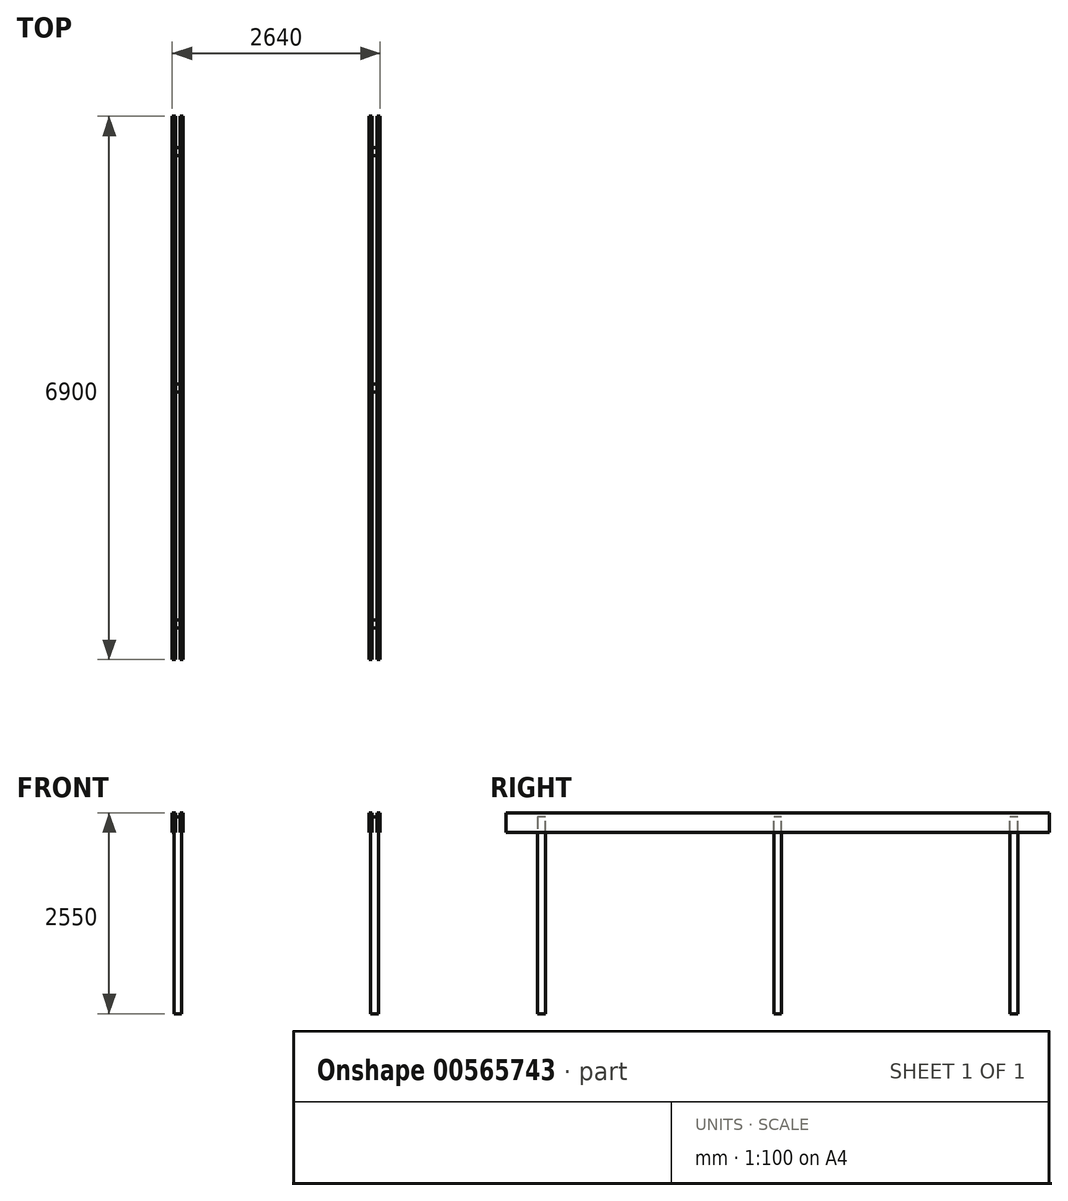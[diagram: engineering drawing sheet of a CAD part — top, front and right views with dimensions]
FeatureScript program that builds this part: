
annotation { "Feature Type Name" : "Feature", "Feature Type Description" : "" }
export const myFeature = defineFeature(function(context is Context, id is Id, definition is map)
    precondition{}
    {
        {
            assignVariable(context, id + "F0", {"name" : "Laenge", "anyValue" : 6000 * mm});
        }
        {
            assignVariable(context, id + "F1", {"name" : "Hoehe", "anyValue" : 2500});
        }
        {
            var Q0;
            Q0=qCreatedBy(makeId("Top.planeOp"),FACE);
            var sketch = newSketch(context, id + "F2", { "sketchPlane" : qUnion([Q0])});
            skLineSegment(sketch, "E0.bottom", {"start": v(-68.16, -102.24) * mm, "end": v(31.84, -102.24) * mm});
            skLineSegment(sketch, "E0.top", {"start": v(-68.16, -2.24) * mm, "end": v(31.84, -2.24) * mm});
            skLineSegment(sketch, "E0.left", {"start": v(-68.16, -102.24) * mm, "end": v(-68.16, -2.24) * mm});
            skLineSegment(sketch, "E0.right", {"start": v(31.84, -102.24) * mm, "end": v(31.84, -2.24) * mm});
            skLineSegment(sketch, "E1.0.1.0", {"start": v(-68.16, 2897.76) * mm, "end": v(-68.16, 2997.76) * mm});
            skLineSegment(sketch, "E1.0.1.1", {"start": v(-68.16, 2997.76) * mm, "end": v(31.84, 2997.76) * mm});
            skLineSegment(sketch, "E1.0.1.2", {"start": v(-68.16, 2897.76) * mm, "end": v(31.84, 2897.76) * mm});
            skLineSegment(sketch, "E1.0.1.3", {"start": v(31.84, 2897.76) * mm, "end": v(31.84, 2997.76) * mm});
            skLineSegment(sketch, "E1.0.2.0", {"start": v(-68.16, 5897.76) * mm, "end": v(-68.16, 5997.76) * mm});
            skLineSegment(sketch, "E1.0.2.1", {"start": v(-68.16, 5997.76) * mm, "end": v(31.84, 5997.76) * mm});
            skLineSegment(sketch, "E1.0.2.2", {"start": v(-68.16, 5897.76) * mm, "end": v(31.84, 5897.76) * mm});
            skLineSegment(sketch, "E1.0.2.3", {"start": v(31.84, 5897.76) * mm, "end": v(31.84, 5997.76) * mm});
            skLineSegment(sketch, "E1.1.0.0", {"start": v(2431.84, -102.24) * mm, "end": v(2431.84, -2.24) * mm});
            skLineSegment(sketch, "E1.1.0.1", {"start": v(2431.84, -2.24) * mm, "end": v(2531.84, -2.24) * mm});
            skLineSegment(sketch, "E1.1.0.2", {"start": v(2431.84, -102.24) * mm, "end": v(2531.84, -102.24) * mm});
            skLineSegment(sketch, "E1.1.0.3", {"start": v(2531.84, -102.24) * mm, "end": v(2531.84, -2.24) * mm});
            skLineSegment(sketch, "E1.1.1.0", {"start": v(2431.84, 2897.76) * mm, "end": v(2431.84, 2997.76) * mm});
            skLineSegment(sketch, "E1.1.1.1", {"start": v(2431.84, 2997.76) * mm, "end": v(2531.84, 2997.76) * mm});
            skLineSegment(sketch, "E1.1.1.2", {"start": v(2431.84, 2897.76) * mm, "end": v(2531.84, 2897.76) * mm});
            skLineSegment(sketch, "E1.1.1.3", {"start": v(2531.84, 2897.76) * mm, "end": v(2531.84, 2997.76) * mm});
            skLineSegment(sketch, "E1.1.2.0", {"start": v(2431.84, 5897.76) * mm, "end": v(2431.84, 5997.76) * mm});
            skLineSegment(sketch, "E1.1.2.1", {"start": v(2431.84, 5997.76) * mm, "end": v(2531.84, 5997.76) * mm});
            skLineSegment(sketch, "E1.1.2.2", {"start": v(2431.84, 5897.76) * mm, "end": v(2531.84, 5897.76) * mm});
            skLineSegment(sketch, "E1.1.2.3", {"start": v(2531.84, 5897.76) * mm, "end": v(2531.84, 5997.76) * mm});
            skLineSegment(sketch, "E1.direction1", {"start": v(-68.16, -102.24) * mm, "end": v(2431.84, -102.24) * mm, "construction": true});
            skLineSegment(sketch, "E1.direction2", {"start": v(-68.16, -102.24) * mm, "end": v(-68.16, 2897.76) * mm, "construction": true});
            skSolve(sketch);
        }
        {
            var Q0;
            Q0=makeQuery(id+"F2.imprint","IMPRINT",FACE,{"disambiguationData":[TD([[makeQuery(id+"F2.imprint","IMPRINT",EDGE,{"derivedFrom":sQuery(id+"F2.wireOp",EDGE,"E0.bottom")}),1.0]])]});
            var Q1;
            Q1=makeQuery(id+"F2.imprint","IMPRINT",FACE,{"disambiguationData":[TD([[makeQuery(id+"F2.imprint","IMPRINT",EDGE,{"derivedFrom":sQuery(id+"F2.wireOp",EDGE,"E1.0.1.0")}),-1.0]])]});
            var Q2;
            Q2=makeQuery(id+"F2.imprint","IMPRINT",FACE,{"disambiguationData":[TD([[makeQuery(id+"F2.imprint","IMPRINT",EDGE,{"derivedFrom":sQuery(id+"F2.wireOp",EDGE,"E1.0.2.0")}),-1.0]])]});
            var Q3;
            Q3=makeQuery(id+"F2.imprint","IMPRINT",FACE,{"disambiguationData":[TD([[makeQuery(id+"F2.imprint","IMPRINT",EDGE,{"derivedFrom":sQuery(id+"F2.wireOp",EDGE,"E1.1.1.0")}),-1.0]])]});
            var Q4;
            Q4=makeQuery(id+"F2.imprint","IMPRINT",FACE,{"disambiguationData":[TD([[makeQuery(id+"F2.imprint","IMPRINT",EDGE,{"derivedFrom":sQuery(id+"F2.wireOp",EDGE,"E1.1.0.0")}),-1.0]])]});
            var Q5;
            Q5=makeQuery(id+"F2.imprint","IMPRINT",FACE,{"disambiguationData":[TD([[makeQuery(id+"F2.imprint","IMPRINT",EDGE,{"derivedFrom":sQuery(id+"F2.wireOp",EDGE,"E1.1.2.0")}),-1.0]])]});
            extrude(context, id + "F3", {"entities" : qUnion([Q0, Q1, Q2, Q3, Q4, Q5]), "depth" : (getVariable(context, 'Hoehe')) * mm, "offsetDistance" : 25 * mm});
        }
        {
            var Q0;
            Q0=makeQuery(id+"F3.opExtrude","SWEPT_FACE",FACE,{"disambiguationData":[OSD([sQuery(id+"F2.wireOp",EDGE,"E1.1.0.2")])]});
            var sketch = newSketch(context, id + "F4", { "sketchPlane" : qUnion([Q0])});
            skPoint(sketch, "E2.0", {"position": v(2481.84, 2500) * mm});
            skLineSegment(sketch, "E3.0", {"start": v(2531.84, 2500) * mm, "end": v(2531.84, 0) * mm});
            skLineSegment(sketch, "E4.0", {"start": v(2431.84, 2500) * mm, "end": v(2431.84, 0) * mm});
            skLineSegment(sketch, "E5.0", {"start": v(-68.16, 2500) * mm, "end": v(-68.16, 0) * mm});
            skLineSegment(sketch, "E6.0.0", {"start": v(-68.16, 0) * mm, "end": v(31.84, 0) * mm});
            skLineSegment(sketch, "E6.0.1", {"start": v(31.84, 0) * mm, "end": v(31.84, 2500) * mm});
            skLineSegment(sketch, "E6.0.2", {"start": v(31.84, 2500) * mm, "end": v(-68.16, 2500) * mm});
            skLineSegment(sketch, "E7.0.3", {"start": v(31.84, 2500) * mm, "end": v(31.84, 0) * mm});
            skLineSegment(sketch, "E8.bottom", {"start": v(2531.84, 2500) * mm, "end": v(2511.84, 2500) * mm});
            skLineSegment(sketch, "E8.top", {"start": v(2531.84, 2300) * mm, "end": v(2511.84, 2300) * mm});
            skLineSegment(sketch, "E8.left", {"start": v(2531.84, 2500) * mm, "end": v(2531.84, 2300) * mm});
            skLineSegment(sketch, "E8.right", {"start": v(2511.84, 2500) * mm, "end": v(2511.84, 2300) * mm});
            skLineSegment(sketch, "E9", {"start": v(2481.84, 2500) * mm, "end": v(2481.84, 2450.1) * mm, "construction": true});
            skLineSegment(sketch, "E10.MirrorCS", {"start": v(2451.84, 2500) * mm, "end": v(2451.84, 2300) * mm});
            skLineSegment(sketch, "E11.MirrorCS", {"start": v(2431.84, 2300) * mm, "end": v(2451.84, 2300) * mm});
            skLineSegment(sketch, "E12", {"start": v(31.84, 2500) * mm, "end": v(2431.84, 2500) * mm, "construction": true});
            skLineSegment(sketch, "E13", {"start": v(1231.84, 2500) * mm, "end": v(1231.84, 2270.8) * mm, "construction": true});
            skLineSegment(sketch, "E14.MirrorCS", {"start": v(11.84, 2500) * mm, "end": v(11.84, 2300) * mm});
            skLineSegment(sketch, "E15.MirrorCS", {"start": v(31.84, 2300) * mm, "end": v(11.84, 2300) * mm});
            skLineSegment(sketch, "E16.MirrorCS", {"start": v(-48.16, 2500) * mm, "end": v(-48.16, 2300) * mm});
            skLineSegment(sketch, "E17.MirrorCS", {"start": v(-68.16, 2300) * mm, "end": v(-48.16, 2300) * mm});
            skSolve(sketch);
        }
        {
            var Q0;
            {var subQ3=sQuery(id+"F4.wireOp",EDGE,"E16.MirrorCS");Q0=makeQuery(id+"F4.imprint","IMPRINT",FACE,{"disambiguationData":[TD([[makeQuery(id+"F4.imprint","IMPRINT",EDGE,{"derivedFrom":subQ3}),-1.0]])]});}
            var Q1;
            {var subQ3=sQuery(id+"F4.wireOp",EDGE,"E14.MirrorCS");Q1=makeQuery(id+"F4.imprint","IMPRINT",FACE,{"disambiguationData":[TD([[makeQuery(id+"F4.imprint","IMPRINT",EDGE,{"derivedFrom":subQ3}),1.0]])]});}
            var Q2;
            {var subQ4=sQuery(id+"F4.wireOp",EDGE,"E10.MirrorCS");Q2=makeQuery(id+"F4.imprint","IMPRINT",FACE,{"disambiguationData":[TD([[makeQuery(id+"F4.imprint","IMPRINT",EDGE,{"derivedFrom":subQ4}),-1.0]])]});}
            var Q3;
            Q3=makeQuery(id+"F4.imprint","IMPRINT",FACE,{"disambiguationData":[TD([[makeQuery(id+"F4.imprint","IMPRINT",EDGE,{"derivedFrom":sQuery(id+"F4.wireOp",EDGE,"E8.bottom")}),-1.0]])]});
            extrude(context, id + "F5", {"entities" : qUnion([Q0, Q1, Q2, Q3]), "operationType" : NewBodyOperationType.REMOVE, "endBound" : BoundingType.THROUGH_ALL, "oppositeDirection" : true, "depth" : 25 * mm, "offsetDistance" : 25 * mm});
        }
        {
            var Q0;
            Q0=makeQuery(id+"F3.opExtrude","SWEPT_FACE",FACE,{"disambiguationData":[OSD([sQuery(id+"F2.wireOp",EDGE,"E1.1.0.2")])]});
            var sketch = newSketch(context, id + "F6", { "sketchPlane" : qUnion([Q0])});
            skPoint(sketch, "E18.0", {"position": v(2511.84, 2300) * mm});
            skLineSegment(sketch, "E19.bottom", {"start": v(2511.84, 2300) * mm, "end": v(2551.84, 2300) * mm});
            skLineSegment(sketch, "E19.top", {"start": v(2511.84, 2550) * mm, "end": v(2551.84, 2550) * mm});
            skLineSegment(sketch, "E19.left", {"start": v(2511.84, 2300) * mm, "end": v(2511.84, 2550) * mm});
            skLineSegment(sketch, "E19.right", {"start": v(2551.84, 2300) * mm, "end": v(2551.84, 2550) * mm});
            skLineSegment(sketch, "E20.MirrorCS", {"start": v(-48.16, 2300) * mm, "end": v(-48.16, 2550) * mm});
            skLineSegment(sketch, "E21.MirrorCS", {"start": v(-48.16, 2300) * mm, "end": v(-88.16, 2300) * mm});
            skLineSegment(sketch, "E22.MirrorCS", {"start": v(-88.16, 2300) * mm, "end": v(-88.16, 2550) * mm});
            skLineSegment(sketch, "E23.MirrorCS", {"start": v(-48.16, 2550) * mm, "end": v(-88.16, 2550) * mm});
            skLineSegment(sketch, "E24.MirrorCS", {"start": v(2451.84, 2550) * mm, "end": v(2411.84, 2550) * mm});
            skLineSegment(sketch, "E25.MirrorCS", {"start": v(2451.84, 2300) * mm, "end": v(2451.84, 2550) * mm});
            skLineSegment(sketch, "E26.MirrorCS", {"start": v(2411.84, 2300) * mm, "end": v(2411.84, 2550) * mm});
            skLineSegment(sketch, "E27.MirrorCS", {"start": v(2451.84, 2300) * mm, "end": v(2411.84, 2300) * mm});
            skLineSegment(sketch, "E28.MirrorCS", {"start": v(51.84, 2300) * mm, "end": v(51.84, 2550) * mm});
            skLineSegment(sketch, "E29.MirrorCS", {"start": v(11.84, 2550) * mm, "end": v(51.84, 2550) * mm});
            skLineSegment(sketch, "E30.MirrorCS", {"start": v(11.84, 2300) * mm, "end": v(11.84, 2550) * mm});
            skLineSegment(sketch, "E31.MirrorCS", {"start": v(11.84, 2300) * mm, "end": v(51.84, 2300) * mm});
            skSolve(sketch);
        }
        {
            var Q0;
            {var subQ4=sQuery(id+"F6.wireOp",EDGE,"E24.MirrorCS");Q0=makeQuery(id+"F6.imprint","IMPRINT",FACE,{"disambiguationData":[TD([[makeQuery(id+"F6.imprint","IMPRINT",EDGE,{"derivedFrom":subQ4}),1.0]])]});}
            var Q1;
            {var subQ5=sQuery(id+"F6.wireOp",EDGE,"E19.top");Q1=makeQuery(id+"F6.imprint","IMPRINT",FACE,{"disambiguationData":[TD([[makeQuery(id+"F6.imprint","IMPRINT",EDGE,{"derivedFrom":subQ5}),-1.0]])]});}
            var Q2;
            Q2=makeQuery(id+"F6.imprint","IMPRINT",FACE,{"disambiguationData":[TD([[makeQuery(id+"F6.imprint","IMPRINT",EDGE,{"derivedFrom":sQuery(id+"F6.wireOp",EDGE,"E20.MirrorCS")}),1.0]])]});
            var Q3;
            Q3=makeQuery(id+"F6.imprint","IMPRINT",FACE,{"disambiguationData":[TD([[makeQuery(id+"F6.imprint","IMPRINT",EDGE,{"derivedFrom":sQuery(id+"F6.wireOp",EDGE,"E28.MirrorCS")}),1.0]])]});
            extrude(context, id + "F7", {"entities" : qUnion([Q0, Q1, Q2, Q3]), "depth" : 400 * mm, "offsetDistance" : 25 * mm, "hasSecondDirection" : true, "secondDirectionOppositeDirection" : true, "secondDirectionDepth" : getVariable(context, 'Laenge') + 500 * mm});
        }
    });
